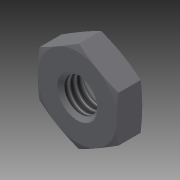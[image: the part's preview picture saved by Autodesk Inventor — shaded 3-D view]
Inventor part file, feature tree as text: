
AUTODESK INVENTOR PART (.ipt)
format: ipt  version: 2014 (Build 180170000, 170)  size: 161,280 bytes
history: native  units: in
note: dims shown in document units (in); Inventor stores cm internally (conversion verified against a paired STEP export)
features: other x70, sketch x3, revolve x2, extrude x1, thread x1
ambient origin geometry x8: Origin, YZ Plane, XZ Plane, XY Plane, X Axis, Y Axis, Z Axis, Center Point
bodies: Solid1 (feature_tree)
feature tree (77):
  sketch  "Sketch_8"  dims[d0=360.0deg d1=0.12in d2=0.0in]
  sketch  "Sketch_10"  dims[d3=360.0deg d4=0.0862in d5=0.0in]
  revolve  "Revolution1"  [1 undecoded]
  extrude  "Extrusion1"  Depth=0.0862in TaperAngle=0.0deg
  revolve  "Revolution2"  [1 undecoded]
  thread  "Thread1"  [1 undecoded]
  other  "NUT_XY"
  other  "NUT_YZ"
  other  "NUT_ZX"
  other  "NUT_X"
  other  "NUT_Y"
  other  "NUT_Z"
  other  "NUT_Center"
  other  "a1_XY"
  other  "a1_YZ"
  other  "a1_ZX"
  other  "a1_X"
  other  "a1_Y"
  other  "a1_Z"
  other  "a1_Center"
  other  "a2_XY"
  other  "a2_YZ"
  other  "a2_ZX"
  other  "a2_X"
  other  "a2_Y"
  other  "a2_Z"
  other  "a2_Center"
  other  "b1_XY"
  other  "b1_YZ"
  other  "b1_ZX"
  other  "b1_X"
  other  "b1_Y"
  other  "b1_Z"
  other  "b1_Center"
  other  "b2_XY"
  other  "b2_YZ"
  other  "b2_ZX"
  other  "b2_X"
  other  "b2_Y"
  other  "b2_Z"
  other  "b2_Center"
  other  "e_XY"
  other  "e_YZ"
  other  "e_ZX"
  other  "e_X"
  other  "e_Y"
  other  "e_Z"
  other  "e_Center"
  other  "ol1_XY"
  other  "ol1_YZ"
  other  "ol1_ZX"
  other  "ol1_X"
  other  "ol1_Y"
  other  "ol1_Z"
  other  "ol1_Center"
  other  "ol2_XY"
  other  "ol2_YZ"
  other  "ol2_ZX"
  other  "ol2_X"
  other  "ol2_Y"
  other  "ol2_Z"
  other  "ol2_Center"
  other  "th1_XY"
  other  "th1_YZ"
  other  "th1_ZX"
  other  "th1_X"
  other  "th1_Y"
  other  "th1_Z"
  other  "th1_Center"
  other  "th2_XY"
  other  "th2_YZ"
  other  "th2_ZX"
  other  "th2_X"
  other  "th2_Y"
  other  "th2_Z"
  other  "th2_Center"
  sketch  "Sketch_11"
note: 3 required parameter values undecoded (feature->parameter linkage not recoverable at this tier; creation-order binding heuristic only, values carry confidence <= 0.55)